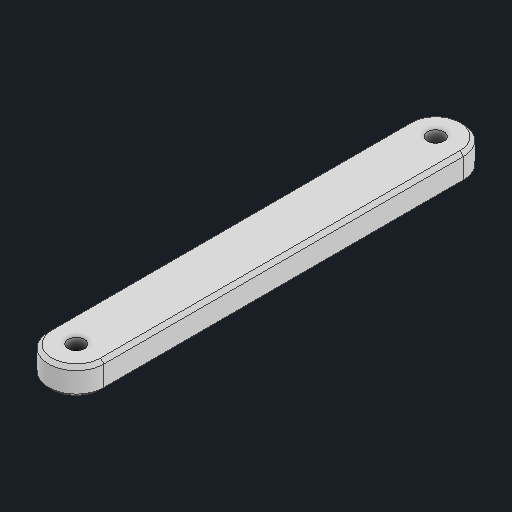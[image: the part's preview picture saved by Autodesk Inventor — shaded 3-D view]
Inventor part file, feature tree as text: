
AUTODESK INVENTOR PART (.ipt)
format: ipt  version: 2025.1 (Build 291241020, 241B)  size: 110,592 bytes
history: native  units: in
note: dims shown in document units (in); Inventor stores cm internally (conversion verified against a paired STEP export)
features: extrude x1, fillet x1, chamfer x1, sketch x1
ambient origin geometry x8: Origin, YZ Plane, XZ Plane, XY Plane, X Axis, Y Axis, Z Axis, Center Point
bodies: Solid1 (feature_tree)
feature tree (4):
  extrude  "Extrusion1"  Depth=3.0in
  fillet  "Fillet1"  Radius=0.1181in
  chamfer  "Chamfer1"  Distance=0.1181in
  sketch  "Sketch1"  dims[d0=0.4in d1=3.0in d2=0.1181in d3=0.1181in d4=0.2in d5=0.2in d6=0.1969in d7=0.0in d8=0.2in d9=0.025in d10=0.125in d11=45.0deg]
